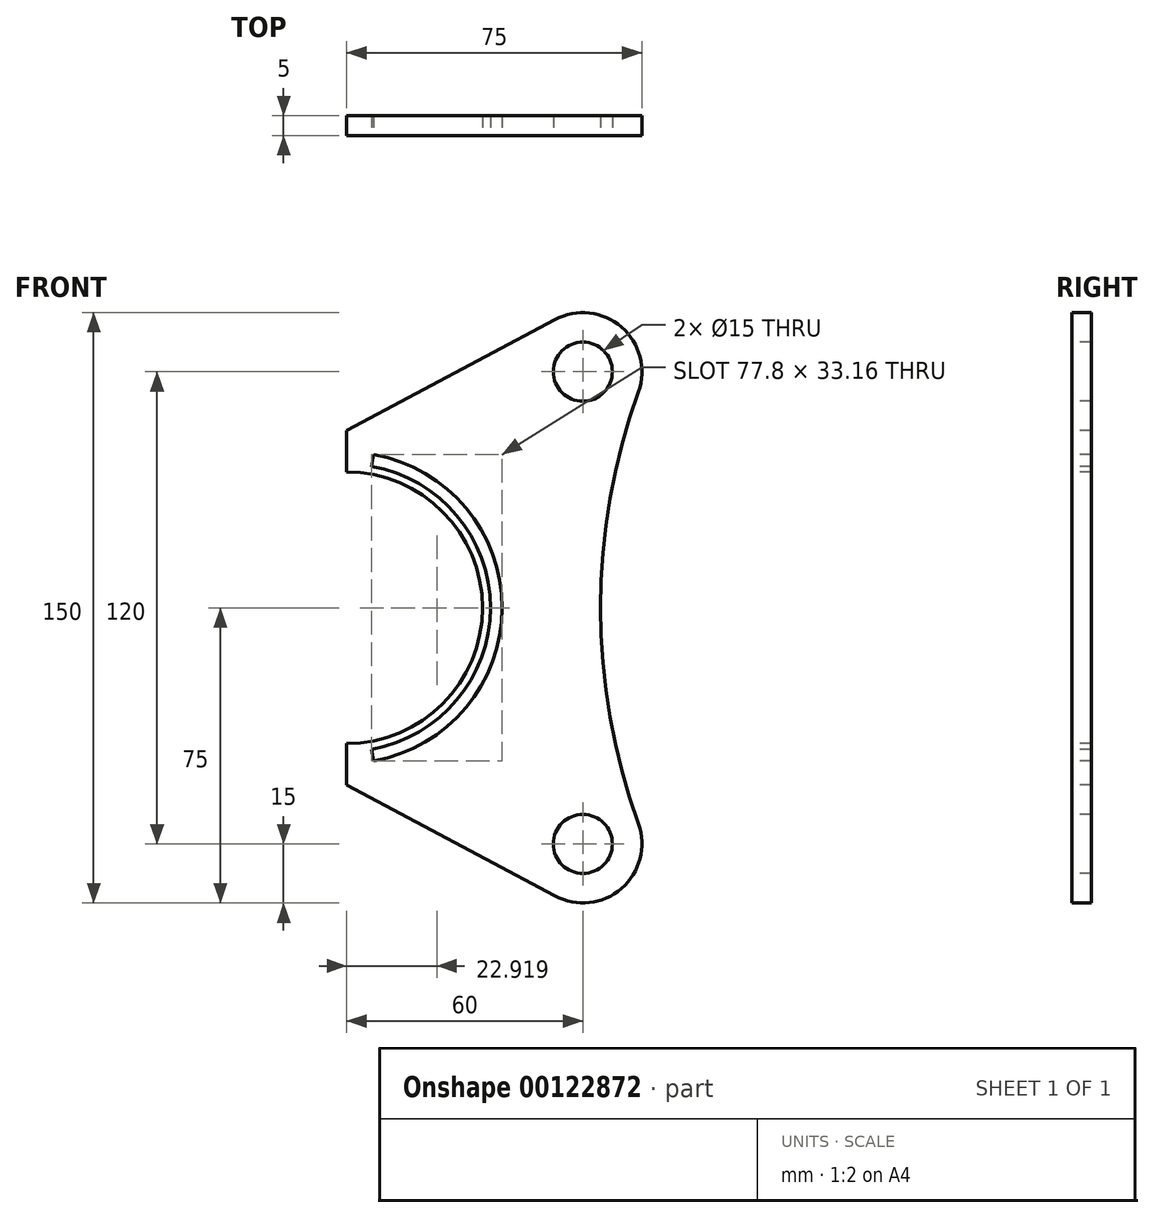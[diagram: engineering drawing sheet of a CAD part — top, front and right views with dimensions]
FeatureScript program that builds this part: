
annotation { "Feature Type Name" : "Feature", "Feature Type Description" : "" }
export const myFeature = defineFeature(function(context is Context, id is Id, definition is map)
    precondition{}
    {
        {
            var Q0;
            Q0=qCreatedBy(makeId("Front.planeOp"),FACE);
            var sketch = newSketch(context, id + "F0", { "sketchPlane" : qUnion([Q0])});
            skArc(sketch, "E0", {"start": v(-700, -34.5) * mm, "mid": v(-665.5, 0) * mm, "end": v(-700, 34.5) * mm});
            skCircle(sketch, "E1", {"center": v(0, 0) * mm, "radius": 642.8 * mm, "construction": true});
            skPoint(sketch, "E2", {"position": v(-640, 60) * mm});
            skPoint(sketch, "E3", {"position": v(-640, -60) * mm});
            skCircle(sketch, "E4", {"center": v(-640, 60) * mm, "radius": 7.5 * mm});
            skCircle(sketch, "E5", {"center": v(-640, -60) * mm, "radius": 7.5 * mm});
            skArc(sketch, "E6", {"start": v(-625.9, 54.9) * mm, "mid": v(-630.18, 71.34) * mm, "end": v(-647.06, 73.24) * mm});
            skArc(sketch, "E7", {"start": v(-647.06, -73.24) * mm, "mid": v(-630.18, -71.34) * mm, "end": v(-625.9, -54.9) * mm});
            skLineSegment(sketch, "E8", {"start": v(-700, 45) * mm, "end": v(-647.06, 73.24) * mm});
            skLineSegment(sketch, "E9", {"start": v(-647.06, -73.24) * mm, "end": v(-700, -45) * mm});
            skLineSegment(sketch, "E10", {"start": v(-700, -91.27) * mm, "end": v(-700, 112.6) * mm, "construction": true});
            skArc(sketch, "E11", {"start": v(-693.66, -35.95) * mm, "mid": v(-663.5, 0) * mm, "end": v(-693.66, 35.95) * mm});
            skArc(sketch, "E12", {"start": v(-693.14, -38.9) * mm, "mid": v(-660.5, 0) * mm, "end": v(-693.14, 38.9) * mm});
            skLineSegment(sketch, "E13", {"start": v(-700, 45) * mm, "end": v(-700, 34.5) * mm});
            skLineSegment(sketch, "E14", {"start": v(-700, -45) * mm, "end": v(-700, -34.5) * mm});
            skLineSegment(sketch, "E15", {"start": v(-700, 0) * mm, "end": v(-690.13, 55.95) * mm, "construction": true});
            skLineSegment(sketch, "E16", {"start": v(-700, 0) * mm, "end": v(-689.73, -58.24) * mm, "construction": true});
            skLineSegment(sketch, "E17", {"start": v(-693.66, -35.95) * mm, "end": v(-693.14, -38.9) * mm});
            skLineSegment(sketch, "E18", {"start": v(-693.14, 38.9) * mm, "end": v(-693.66, 35.95) * mm});
            skArc(sketch, "E19", {"start": v(-625.9, 54.9) * mm, "mid": v(-635.5, 0) * mm, "end": v(-625.9, -54.9) * mm});
            skSolve(sketch);
        }
        {
            var Q0;
            Q0=qSketchRegion(id+"F0",true);
            extrude(context, id + "F1", {"entities" : qUnion([Q0]), "oppositeDirection" : true, "depth" : 5 * mm});
        }
    });
